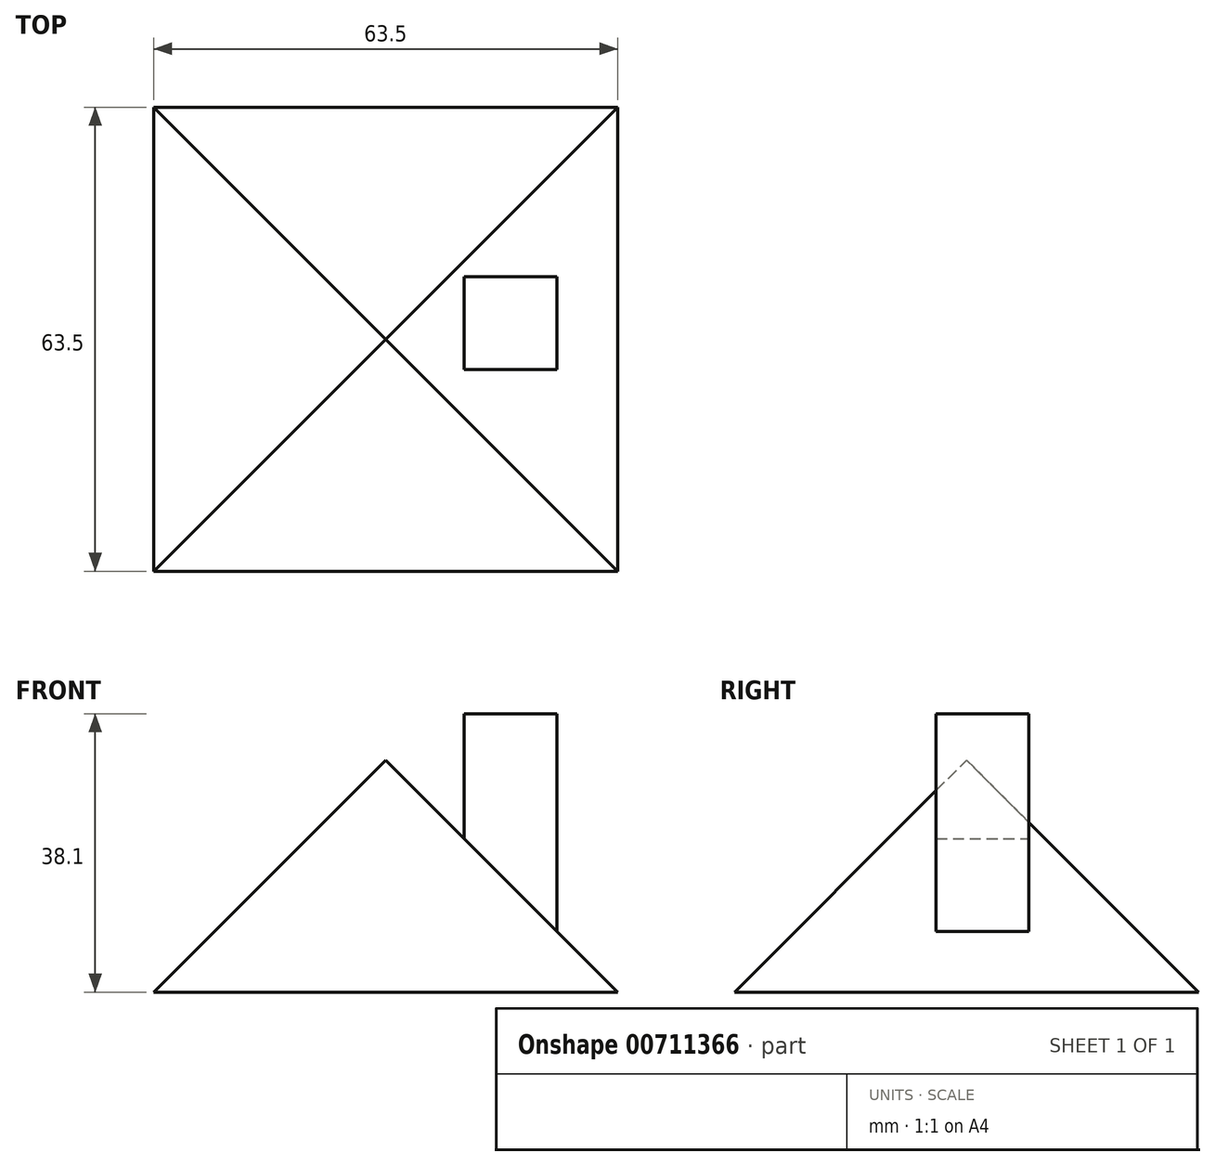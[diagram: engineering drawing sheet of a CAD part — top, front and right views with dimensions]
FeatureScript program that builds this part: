
annotation { "Feature Type Name" : "Feature", "Feature Type Description" : "" }
export const myFeature = defineFeature(function(context is Context, id is Id, definition is map)
    precondition{}
    {
        {
            var Q0;
            Q0=qCreatedBy(makeId("Top.planeOp"),FACE);
            var sketch = newSketch(context, id + "F0", { "sketchPlane" : qUnion([Q0])});
            skLineSegment(sketch, "E0.bottom", {"start": v(-30.76, 30.8) * mm, "end": v(32.74, 30.8) * mm});
            skLineSegment(sketch, "E0.top", {"start": v(-30.76, -32.7) * mm, "end": v(32.74, -32.7) * mm});
            skLineSegment(sketch, "E0.left", {"start": v(-30.76, 30.8) * mm, "end": v(-30.76, -32.7) * mm});
            skLineSegment(sketch, "E0.right", {"start": v(32.74, 30.8) * mm, "end": v(32.74, -32.7) * mm});
            skLineSegment(sketch, "E1.bottom", {"start": v(11.73, 7.6) * mm, "end": v(24.43, 7.6) * mm});
            skLineSegment(sketch, "E1.top", {"start": v(11.73, -5.1) * mm, "end": v(24.43, -5.1) * mm});
            skLineSegment(sketch, "E1.left", {"start": v(11.73, 7.6) * mm, "end": v(11.73, -5.1) * mm});
            skLineSegment(sketch, "E1.right", {"start": v(24.43, 7.6) * mm, "end": v(24.43, -5.1) * mm});
            skSolve(sketch);
        }
        {
            var Q0;
            Q0=makeQuery(id+"F0.imprint","IMPRINT",FACE,{"disambiguationData":[TD([[makeQuery(id+"F0.imprint","IMPRINT",EDGE,{"derivedFrom":sQuery(id+"F0.wireOp",EDGE,"E0.bottom")}),-1.0]])]});
            extrude(context, id + "F1", {"entities" : qUnion([Q0]), "depth" : 31.75 * mm, "offsetDistance" : 25.4 * mm});
        }
        {
            var Q0;
            Q0=makeQuery(id+"F1.opExtrude","CAP_EDGE",EDGE,{"disambiguationData":[OSD([sQuery(id+"F0.wireOp",EDGE,"E0.top")])],"isStart":false});
            var Q1;
            Q1=makeQuery(id+"F1.opExtrude","CAP_EDGE",EDGE,{"disambiguationData":[OSD([sQuery(id+"F0.wireOp",EDGE,"E0.right")])],"isStart":false});
            var Q2;
            Q2=makeQuery(id+"F1.opExtrude","CAP_EDGE",EDGE,{"disambiguationData":[OSD([sQuery(id+"F0.wireOp",EDGE,"E0.bottom")])],"isStart":false});
            var Q3;
            Q3=makeQuery(id+"F1.opExtrude","CAP_EDGE",EDGE,{"disambiguationData":[OSD([sQuery(id+"F0.wireOp",EDGE,"E0.left")])],"isStart":false});
            chamfer(context, id + "F2", {"entities" : qUnion([Q0, Q1, Q2, Q3]), "width" : 31.75 * mm, "tangentPropagation" : true});
        }
        {
            var Q0;
            Q0=makeQuery(id+"F0.imprint","IMPRINT",FACE,{"disambiguationData":[TD([[makeQuery(id+"F0.imprint","IMPRINT",EDGE,{"derivedFrom":sQuery(id+"F0.wireOp",EDGE,"E1.bottom")}),-1.0]])]});
            extrude(context, id + "F3", {"entities" : qUnion([Q0]), "operationType" : NewBodyOperationType.ADD, "depth" : 38.1 * mm, "offsetDistance" : 25.4 * mm});
        }
    });
